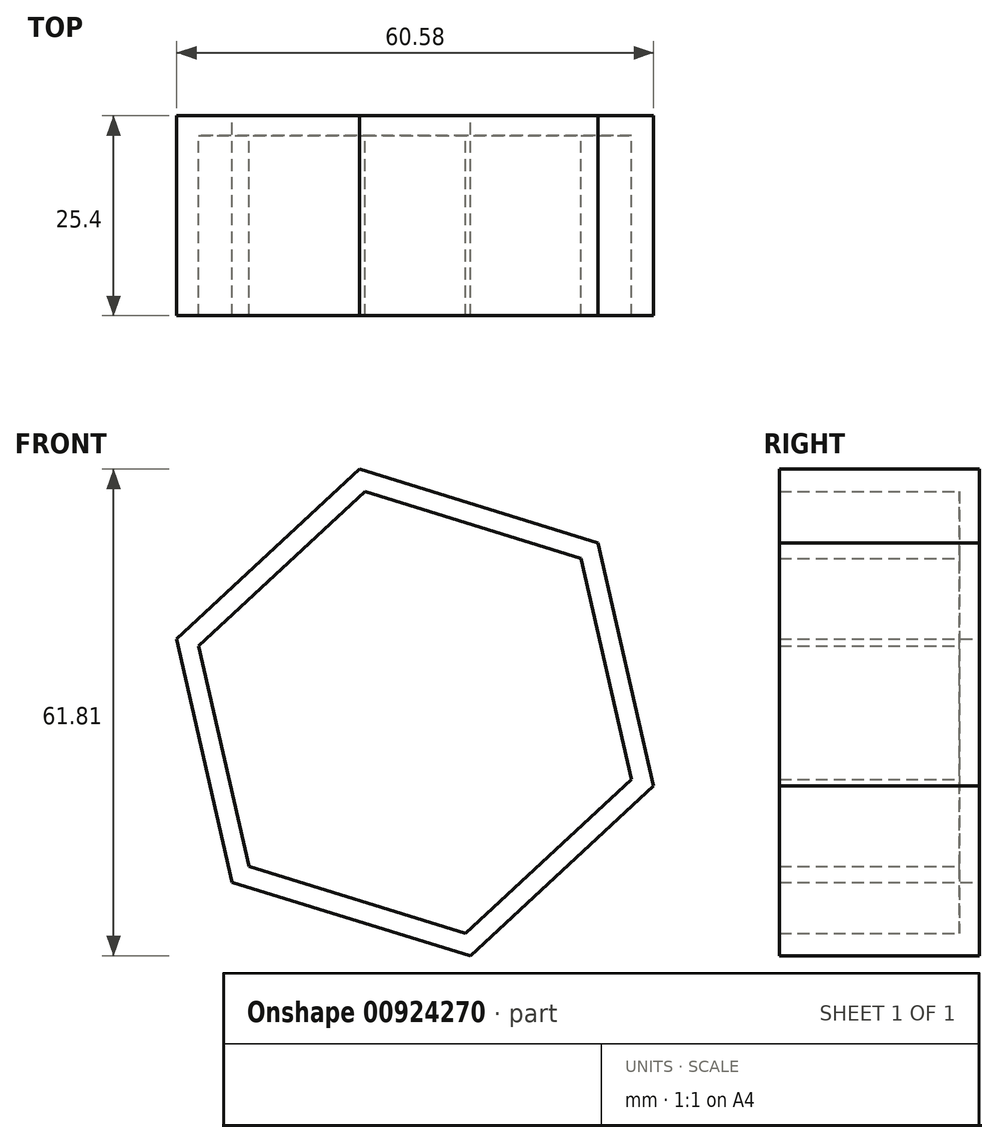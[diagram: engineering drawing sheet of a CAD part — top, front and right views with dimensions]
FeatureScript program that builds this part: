
annotation { "Feature Type Name" : "Feature", "Feature Type Description" : "" }
export const myFeature = defineFeature(function(context is Context, id is Id, definition is map)
    precondition{}
    {
        {
            var Q0;
            Q0=qCreatedBy(makeId("Front.planeOp"),FACE);
            var sketch = newSketch(context, id + "F0", { "sketchPlane" : qUnion([Q0])});
            skCircle(sketch, "E0.cCircle", {"center": v(-17.97, -7.58) * mm, "radius": 31.7 * mm, "construction": true});
            skLineSegment(sketch, "E0.0", {"start": v(5.27, 13.98) * mm, "end": v(12.32, -16.93) * mm});
            skLineSegment(sketch, "E0.1", {"start": v(12.32, -16.93) * mm, "end": v(-10.91, -38.49) * mm});
            skLineSegment(sketch, "E0.2", {"start": v(-10.91, -38.49) * mm, "end": v(-41.2, -29.14) * mm});
            skLineSegment(sketch, "E0.3", {"start": v(-41.2, -29.14) * mm, "end": v(-48.26, 1.76) * mm});
            skLineSegment(sketch, "E0.4", {"start": v(-48.26, 1.76) * mm, "end": v(-25.02, 23.32) * mm});
            skLineSegment(sketch, "E0.5", {"start": v(-25.02, 23.32) * mm, "end": v(5.27, 13.98) * mm});
            skSolve(sketch);
        }
        {
            var Q0;
            Q0=makeQuery(id+"F0.imprint","IMPRINT",FACE,{"disambiguationData":[TD([[makeQuery(id+"F0.imprint","IMPRINT",EDGE,{"derivedFrom":sQuery(id+"F0.wireOp",EDGE,"E0.0")}),-1.0]])]});
            var sketch = newSketch(context, id + "F1", { "sketchPlane" : qUnion([Q0])});
            skSolve(sketch);
        }
        {
            var Q0;
            Q0=makeQuery(id+"F1.imprint","IMPRINT",FACE,{"disambiguationData":[TD([[makeQuery(id+"F1.imprint","IMPRINT",EDGE,{"derivedFrom":makeQuery(id+"F0.imprint","IMPRINT",EDGE,{"derivedFrom":sQuery(id+"F0.wireOp",EDGE,"E0.0")})}),-1.0]])]});
            extrude(context, id + "F2", {"entities" : qUnion([Q0]), "depth" : 25.4 * mm, "offsetDistance" : 25.4 * mm});
        }
        {
            var Q0;
            Q0=makeQuery(id+"F2.opExtrude","CAP_FACE",FACE,{"disambiguationData":[OSD([sQuery(id+"F0.wireOp",EDGE,"E0.0"),sQuery(id+"F0.wireOp",EDGE,"E0.1"),sQuery(id+"F0.wireOp",EDGE,"E0.2"),sQuery(id+"F0.wireOp",EDGE,"E0.3"),sQuery(id+"F0.wireOp",EDGE,"E0.4"),sQuery(id+"F0.wireOp",EDGE,"E0.5")])],"isStart":false});
            shell(context, id + "F3", {"entities" : qUnion([Q0]), "thickness" : 2.54 * mm});
        }
    });
